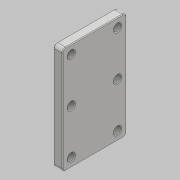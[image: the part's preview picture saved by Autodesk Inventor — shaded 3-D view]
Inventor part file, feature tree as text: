
AUTODESK INVENTOR PART (.ipt)
format: ipt  version: 2018 (Build 220112000, 112)  size: 145,920 bytes
history: native  units: mm
features: chamfer x2, sketch x2, other x1, extrude x1, fillet x1, hole x1, pattern_linear x1, plane x1, mirror x1
ambient origin geometry x8: Origin, YZ Plane, XZ Plane, XY Plane, X Axis, Y Axis, Z Axis, Center Point
bodies: Body1 (feature_tree)
feature tree (11):
  other  "實體1"
  extrude  "擠出1"  Depth=180.0mm
  fillet  "圓角1"  Radius=300.0mm
  chamfer  "倒角1"  Distance=25.0mm
  hole  "孔1"  [1 undecoded]
  chamfer  "倒角2"  Distance=2.0mm Angle=45.0deg
  pattern_linear  "矩形陣列1"  Spacing1=125.0mm  [1 undecoded]
  plane  "工作平面1"
  mirror  "鏡射1"
  sketch  "草圖1"
  sketch  "草圖2"
note: 2 required parameter values undecoded (feature->parameter linkage not recoverable at this tier; creation-order binding heuristic only, values carry confidence <= 0.55)
